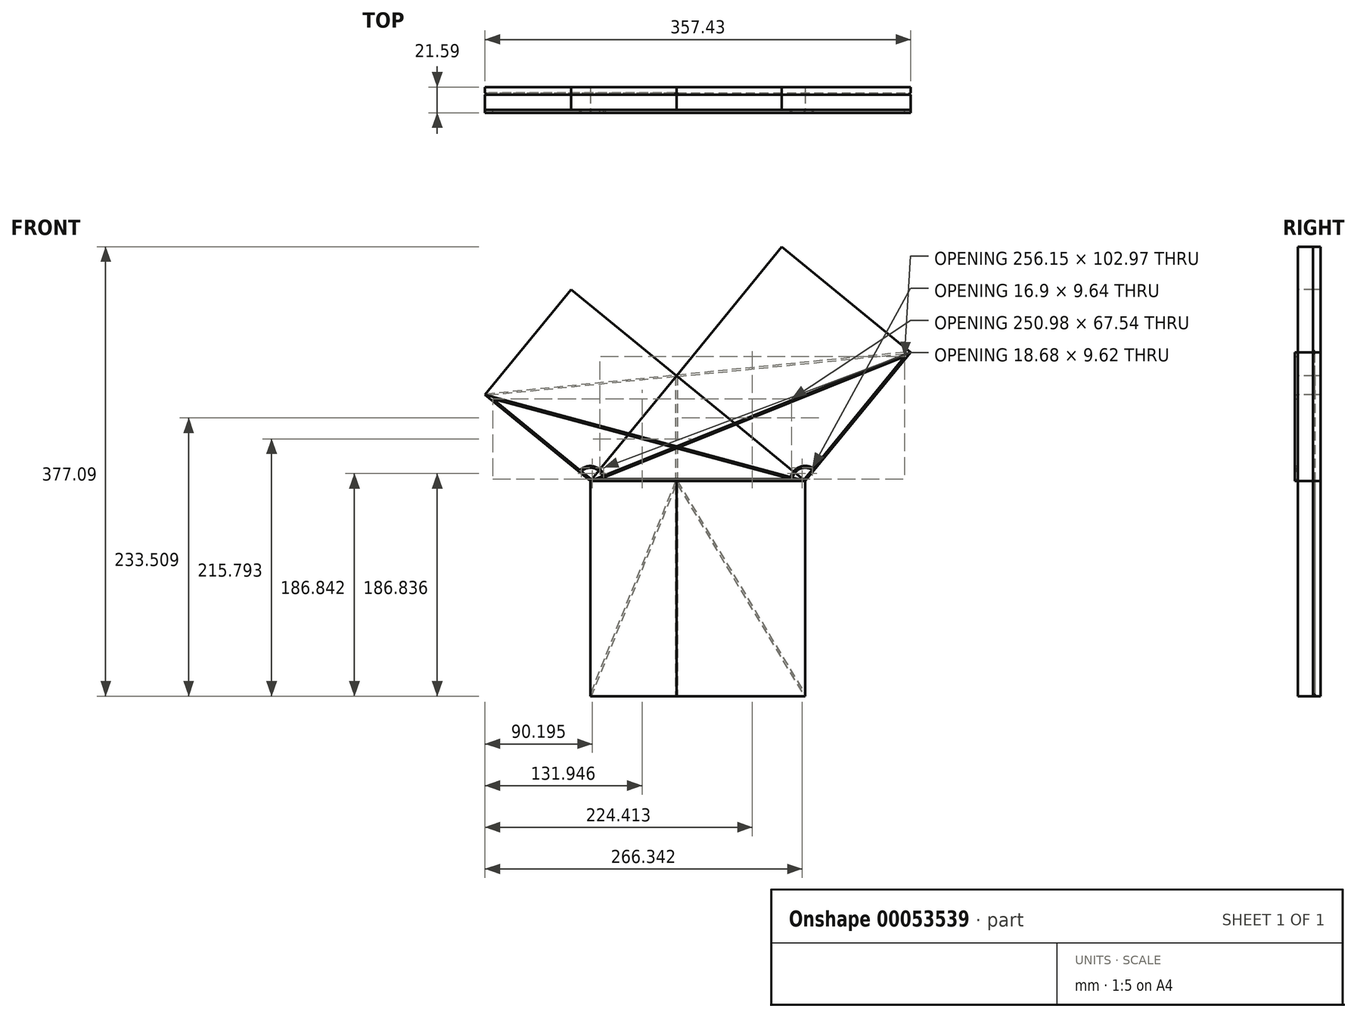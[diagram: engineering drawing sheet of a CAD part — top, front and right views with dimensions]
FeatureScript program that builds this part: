
annotation { "Feature Type Name" : "Feature", "Feature Type Description" : "" }
export const myFeature = defineFeature(function(context is Context, id is Id, definition is map)
    precondition{}
    {
        {
            var Q0;
            Q0=qCreatedBy(makeId("Front.planeOp"),FACE);
            var sketch = newSketch(context, id + "F0", { "sketchPlane" : qUnion([Q0])});
            skLineSegment(sketch, "E0", {"start": v(-72.38, 0) * mm, "end": v(0, 88.46) * mm});
            skLineSegment(sketch, "E1", {"start": v(0, 88.46) * mm, "end": v(108.12, 0) * mm});
            skLineSegment(sketch, "E2", {"start": v(108.12, 0) * mm, "end": v(0, 0) * mm});
            skLineSegment(sketch, "E3", {"start": v(0, 88.46) * mm, "end": v(0, 0) * mm, "construction": true});
            skLineSegment(sketch, "E4.rect.bottom", {"start": v(-72.38, 0) * mm, "end": v(108.12, 0) * mm});
            skLineSegment(sketch, "E4.rect.top", {"start": v(0, -180.5) * mm, "end": v(108.12, -180.5) * mm});
            skLineSegment(sketch, "E4.rect.left", {"start": v(0, 0) * mm, "end": v(0, -180.5) * mm});
            skLineSegment(sketch, "E5.rect.top", {"start": v(0, -180.5) * mm, "end": v(-72.38, -180.5) * mm});
            skLineSegment(sketch, "E5.rect.right", {"start": v(-72.38, 0) * mm, "end": v(-72.38, -180.5) * mm});
            skLineSegment(sketch, "E6", {"start": v(0, 88.46) * mm, "end": v(88.46, 196.59) * mm});
            skLineSegment(sketch, "E7", {"start": v(88.46, 196.59) * mm, "end": v(196.59, 108.12) * mm});
            skLineSegment(sketch, "E8", {"start": v(196.59, 108.12) * mm, "end": v(108.12, 0) * mm});
            skLineSegment(sketch, "E9", {"start": v(0, 88.46) * mm, "end": v(-88.46, 160.84) * mm});
            skLineSegment(sketch, "E10", {"start": v(-88.46, 160.84) * mm, "end": v(-160.84, 72.38) * mm});
            skLineSegment(sketch, "E11", {"start": v(-160.84, 72.38) * mm, "end": v(-72.38, 0) * mm});
            skLineSegment(sketch, "E12", {"start": v(-160.84, 72.38) * mm, "end": v(108.12, 0) * mm, "construction": true});
            skLineSegment(sketch, "E13", {"start": v(196.59, 108.12) * mm, "end": v(-72.38, 0) * mm, "construction": true});
            skLineSegment(sketch, "E14", {"start": v(108.12, 0) * mm, "end": v(108.12, -180.5) * mm});
            skSolve(sketch);
        }
        {
            var Q0;
            {var subQ0=sQuery(id+"F0.wireOp",EDGE,"E0");Q0=makeQuery(id+"F0.imprint","IMPRINT",FACE,{"disambiguationData":[TD([[makeQuery(id+"F0.imprint","IMPRINT",EDGE,{"derivedFrom":subQ0}),-1.0]])]});}
            extrude(context, id + "F1", {"entities" : qUnion([Q0]), "oppositeDirection" : true, "depth" : 12.7 * mm});
        }
        {
            var Q0;
            Q0=makeQuery(id+"F1.opExtrude","CAP_FACE",FACE,{"disambiguationData":[OSD([sQuery(id+"F0.wireOp",EDGE,"E0"),sQuery(id+"F0.wireOp",EDGE,"E1"),sQuery(id+"F0.wireOp",EDGE,"E4.rect.bottom")])],"isStart":false});
            var sketch = newSketch(context, id + "F2", { "sketchPlane" : qUnion([Q0])});
            skLineSegment(sketch, "E15", {"start": v(-108.12, 0) * mm, "end": v(-196.59, 108.12) * mm});
            skLineSegment(sketch, "E16", {"start": v(-196.59, 108.12) * mm, "end": v(-88.46, 196.59) * mm});
            skLineSegment(sketch, "E17", {"start": v(-88.46, 196.59) * mm, "end": v(0, 88.46) * mm});
            skLineSegment(sketch, "E18", {"start": v(0, 88.46) * mm, "end": v(88.46, 160.84) * mm});
            skLineSegment(sketch, "E19", {"start": v(88.46, 160.84) * mm, "end": v(160.84, 72.38) * mm});
            skLineSegment(sketch, "E20", {"start": v(160.84, 72.38) * mm, "end": v(72.38, 0) * mm});
            skLineSegment(sketch, "E21", {"start": v(72.38, 0) * mm, "end": v(72.38, -180.5) * mm});
            skLineSegment(sketch, "E22", {"start": v(72.38, -180.5) * mm, "end": v(-108.12, -180.5) * mm});
            skLineSegment(sketch, "E23", {"start": v(-108.12, -180.5) * mm, "end": v(-108.12, 0) * mm});
            skSolve(sketch);
        }
        {
            var Q0;
            Q0 = qSketchRegion(id + "F2", true);
            extrude(context, id + "F3", {"entities" : qUnion([Q0]), "depth" : 6.35 * mm});
        }
        {
            var Q0;
            Q0=makeQuery(id+"F0.imprint","IMPRINT",FACE,{"disambiguationData":[TD([[makeQuery(id+"F0.imprint","IMPRINT",EDGE,{"derivedFrom":sQuery(id+"F0.wireOp",EDGE,"E0")}),1.0]])]});
            extrude(context, id + "F4", {"entities" : qUnion([Q0]), "oppositeDirection" : true, "depth" : 12.7 * mm});
        }
        {
            var Q0;
            Q0=makeQuery(id+"F0.imprint","IMPRINT",FACE,{"disambiguationData":[TD([[makeQuery(id+"F0.imprint","IMPRINT",EDGE,{"derivedFrom":sQuery(id+"F0.wireOp",EDGE,"E5.rect.top")}),-1.0]])]});
            extrude(context, id + "F5", {"entities" : qUnion([Q0]), "oppositeDirection" : true, "depth" : 12.7 * mm});
        }
        {
            var Q0;
            Q0=makeQuery(id+"F0.imprint","IMPRINT",FACE,{"disambiguationData":[TD([[makeQuery(id+"F0.imprint","IMPRINT",EDGE,{"derivedFrom":sQuery(id+"F0.wireOp",EDGE,"E1")}),1.0]])]});
            extrude(context, id + "F6", {"entities" : qUnion([Q0]), "oppositeDirection" : true, "depth" : 12.7 * mm});
        }
        {
            var Q0;
            Q0=makeQuery(id+"F0.imprint","IMPRINT",FACE,{"disambiguationData":[TD([[makeQuery(id+"F0.imprint","IMPRINT",EDGE,{"derivedFrom":sQuery(id+"F0.wireOp",EDGE,"E4.rect.top")}),1.0]])]});
            extrude(context, id + "F7", {"entities" : qUnion([Q0]), "oppositeDirection" : true, "depth" : 12.7 * mm});
        }
        {
            var Q0;
            Q0=qCreatedBy(makeId("Front.planeOp"),FACE);
            var sketch = newSketch(context, id + "F8", { "sketchPlane" : qUnion([Q0])});
            skLineSegment(sketch, "E24", {"start": v(-72.38, 0) * mm, "end": v(108.12, 0) * mm});
            skLineSegment(sketch, "E25", {"start": v(108.12, 0) * mm, "end": v(-160.84, 72.38) * mm});
            skLineSegment(sketch, "E26", {"start": v(-160.84, 72.38) * mm, "end": v(-72.38, 0) * mm});
            skLineSegment(sketch, "E27.0", {"start": v(96.6, 1.52) * mm, "end": v(-154.38, 69.06) * mm});
            skLineSegment(sketch, "E27.1", {"start": v(-71.84, 1.52) * mm, "end": v(-61.3, 1.52) * mm});
            skLineSegment(sketch, "E27.2", {"start": v(-154.38, 69.06) * mm, "end": v(-81.17, 9.16) * mm});
            skArc(sketch, "E28", {"start": v(-81.17, 9.16) * mm, "mid": v(-68.1, 11.96) * mm, "end": v(-59.77, 1.52) * mm});
            skArc(sketch, "E29.0", {"start": v(-79.98, 8.2) * mm, "mid": v(-68.62, 10.53) * mm, "end": v(-61.3, 1.52) * mm});
            skLineSegment(sketch, "E30.trimOffspring", {"start": v(-79.98, 8.2) * mm, "end": v(-71.84, 1.52) * mm});
            skLineSegment(sketch, "E31.trimOffspring", {"start": v(-59.77, 1.52) * mm, "end": v(96.6, 1.52) * mm});
            skSolve(sketch);
        }
        {
            var Q0;
            Q0 = qSketchRegion(id + "F8", true);
            extrude(context, id + "F9", {"entities" : qUnion([Q0]), "depth" : 2.54 * mm});
        }
        {
            var Q0;
            {var subQ0=sQuery(id+"F0.wireOp",EDGE,"E0");Q0=makeQuery(id+"F0.imprint","IMPRINT",FACE,{"disambiguationData":[TD([[makeQuery(id+"F0.imprint","IMPRINT",EDGE,{"derivedFrom":subQ0}),-1.0]])]});}
            var sketch = newSketch(context, id + "F10", { "sketchPlane" : qUnion([Q0])});
            skLineSegment(sketch, "E32", {"start": v(108.12, 0) * mm, "end": v(196.59, 108.12) * mm});
            skLineSegment(sketch, "E33", {"start": v(196.59, 108.12) * mm, "end": v(-72.38, 0) * mm});
            skLineSegment(sketch, "E34", {"start": v(-72.38, 0) * mm, "end": v(108.12, 0) * mm});
            skLineSegment(sketch, "E35.0", {"start": v(107.4, 1.52) * mm, "end": v(113.95, 9.53) * mm});
            skLineSegment(sketch, "E35.1", {"start": v(-64.5, 1.52) * mm, "end": v(95.51, 1.52) * mm});
            skLineSegment(sketch, "E35.2", {"start": v(191.65, 104.5) * mm, "end": v(-64.5, 1.52) * mm});
            skArc(sketch, "E36", {"start": v(114.93, 10.72) * mm, "mid": v(102.68, 11.48) * mm, "end": v(95.51, 1.52) * mm});
            skArc(sketch, "E37.0", {"start": v(113.95, 9.53) * mm, "mid": v(103.34, 10.1) * mm, "end": v(97.05, 1.52) * mm});
            skLineSegment(sketch, "E38.trimOffspring", {"start": v(97.05, 1.52) * mm, "end": v(107.4, 1.52) * mm});
            skLineSegment(sketch, "E39.trimOffspring", {"start": v(114.93, 10.72) * mm, "end": v(191.65, 104.5) * mm});
            skSolve(sketch);
        }
        {
            var Q0;
            Q0 = qSketchRegion(id + "F10", true);
            extrude(context, id + "F11", {"entities" : qUnion([Q0]), "depth" : 2.54 * mm});
        }
        {
            var Q0;
            Q0=makeQuery(id+"F3.opExtrude","CAP_FACE",FACE,{"disambiguationData":[OSD([sQuery(id+"F2.wireOp",EDGE,"E15"),sQuery(id+"F2.wireOp",EDGE,"E16"),sQuery(id+"F2.wireOp",EDGE,"E17"),sQuery(id+"F2.wireOp",EDGE,"E18"),sQuery(id+"F2.wireOp",EDGE,"E19"),sQuery(id+"F2.wireOp",EDGE,"E20"),sQuery(id+"F2.wireOp",EDGE,"E21"),sQuery(id+"F2.wireOp",EDGE,"E22"),sQuery(id+"F2.wireOp",EDGE,"E23")])],"isStart":true});
            var sketch = newSketch(context, id + "F12", { "sketchPlane" : qUnion([Q0])});
            skLineSegment(sketch, "E40", {"start": v(0, 88.46) * mm, "end": v(0, -180.5) * mm, "construction": true});
            skLineSegment(sketch, "E41", {"start": v(0, 0) * mm, "end": v(-72.38, -180.5) * mm, "construction": true});
            skLineSegment(sketch, "E42", {"start": v(0, 0) * mm, "end": v(108.12, -180.5) * mm, "construction": true});
            skLineSegment(sketch, "E43", {"start": v(0, 88.46) * mm, "end": v(-160.84, 72.38) * mm, "construction": true});
            skLineSegment(sketch, "E44", {"start": v(0, 88.46) * mm, "end": v(196.59, 108.12) * mm, "construction": true});
            skArc(sketch, "E45.0.startCap", {"start": v(-0.08, 89.22) * mm, "mid": v(0.76, 88.54) * mm, "end": v(0.08, 87.7) * mm});
            skArc(sketch, "E45.0.endCap", {"start": v(-160.77, 71.62) * mm, "mid": v(-161.6, 72.3) * mm, "end": v(-160.92, 73.14) * mm});
            skLineSegment(sketch, "E45.0.left", {"start": v(0.08, 87.7) * mm, "end": v(-160.77, 71.62) * mm});
            skLineSegment(sketch, "E45.0.right", {"start": v(-0.08, 89.22) * mm, "end": v(-160.92, 73.14) * mm});
            skArc(sketch, "E45.1.startCap", {"start": v(0.08, 87.7) * mm, "mid": v(-0.76, 88.39) * mm, "end": v(-0.08, 89.22) * mm});
            skArc(sketch, "E45.1.endCap", {"start": v(196.5, 108.88) * mm, "mid": v(197.34, 108.2) * mm, "end": v(196.66, 107.36) * mm});
            skLineSegment(sketch, "E45.1.left", {"start": v(-0.08, 89.22) * mm, "end": v(196.5, 108.88) * mm});
            skLineSegment(sketch, "E45.1.right", {"start": v(0.08, 87.7) * mm, "end": v(196.66, 107.36) * mm});
            skArc(sketch, "E45.2.startCap", {"start": v(-0.76, 88.46) * mm, "mid": v(0, 89.23) * mm, "end": v(0.76, 88.46) * mm});
            skArc(sketch, "E45.2.endCap", {"start": v(0.76, -180.5) * mm, "mid": v(0, -181.26) * mm, "end": v(-0.76, -180.5) * mm});
            skLineSegment(sketch, "E45.2.left", {"start": v(0.76, 88.46) * mm, "end": v(0.76, -180.5) * mm});
            skLineSegment(sketch, "E45.2.right", {"start": v(-0.76, 88.46) * mm, "end": v(-0.76, -180.5) * mm});
            skArc(sketch, "E45.3.startCap", {"start": v(-0.65, -0.4) * mm, "mid": v(-0.4, 0.65) * mm, "end": v(0.65, 0.4) * mm});
            skArc(sketch, "E45.3.endCap", {"start": v(108.78, -180.1) * mm, "mid": v(108.51, -181.15) * mm, "end": v(107.47, -180.9) * mm});
            skLineSegment(sketch, "E45.3.left", {"start": v(0.65, 0.4) * mm, "end": v(108.78, -180.1) * mm});
            skLineSegment(sketch, "E45.3.right", {"start": v(-0.65, -0.4) * mm, "end": v(107.47, -180.9) * mm});
            skArc(sketch, "E45.4.startCap", {"start": v(-0.7, 0.28) * mm, "mid": v(0.28, 0.7) * mm, "end": v(0.7, -0.28) * mm});
            skArc(sketch, "E45.4.endCap", {"start": v(-71.67, -180.78) * mm, "mid": v(-72.66, -181.2) * mm, "end": v(-73.09, -180.22) * mm});
            skLineSegment(sketch, "E45.4.left", {"start": v(0.7, -0.28) * mm, "end": v(-71.67, -180.78) * mm});
            skLineSegment(sketch, "E45.4.right", {"start": v(-0.7, 0.28) * mm, "end": v(-73.09, -180.22) * mm});
            skSolve(sketch);
        }
        {
            var Q0;
            Q0 = qSketchRegion(id + "F12", true);
            extrude(context, id + "F13", {"entities" : qUnion([Q0]), "operationType" : NewBodyOperationType.REMOVE, "oppositeDirection" : true, "depth" : 1.52 * mm});
        }
    });
